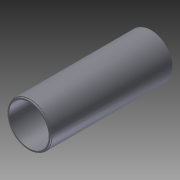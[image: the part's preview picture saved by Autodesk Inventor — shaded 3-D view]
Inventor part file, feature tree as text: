
AUTODESK INVENTOR PART (.ipt)
format: ipt  version: 2011 (Build 150239000, 239)  size: 89,088 bytes
history: native  units: in
note: dims shown in document units (in); Inventor stores cm internally (conversion verified against a paired STEP export)
features: sketch x2, extrude x1, revolve x1, mirror x1
ambient origin geometry x8: Origin, YZ Plane, XZ Plane, XY Plane, X Axis, Y Axis, Z Axis, Center Point
bodies: Solid1 (feature_tree)
feature tree (5):
  extrude  "Extrusion1"  Depth=0.1in
  revolve  "Revolution1"  [1 undecoded]
  mirror  "Mirror1"
  sketch  "Sketch1"  dims[d0=2.062in d1=0.1in]
  sketch  "Sketch2"  dims[d2=5.72in d3=0.0in d4=0.0625in d5=0.031in d6=90.0deg]
note: 1 required parameter value undecoded (feature->parameter linkage not recoverable at this tier; creation-order binding heuristic only, values carry confidence <= 0.55)
